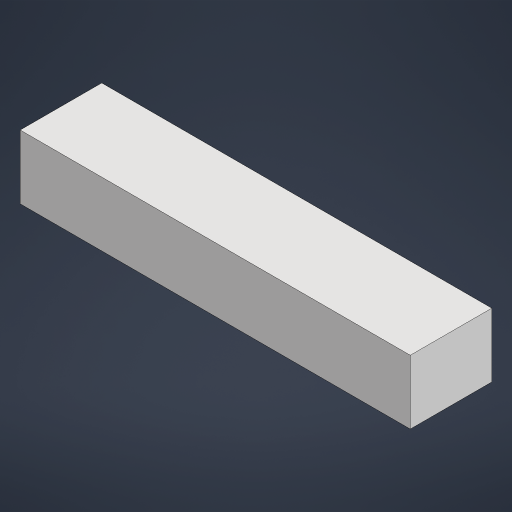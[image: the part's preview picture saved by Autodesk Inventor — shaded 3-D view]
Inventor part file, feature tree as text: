
AUTODESK INVENTOR PART (.ipt)
format: ipt  version: 2023.1 (Build 271208000, 208)  size: 148,480 bytes
history: native  units: in
note: dims shown in document units (in); Inventor stores cm internally (conversion verified against a paired STEP export)
features: extrude x1, sketch x1
ambient origin geometry x8: Origin, YZ Plane, XZ Plane, XY Plane, X Axis, Y Axis, Z Axis, Center Point
bodies: Solid1 (feature_tree)
feature tree (2):
  extrude  "Extrusion1"  Depth=4.625in
  sketch  "Sketch2"  dims[d3=22.125in d4=4.625in d5=3.625in d6=0.0in]
